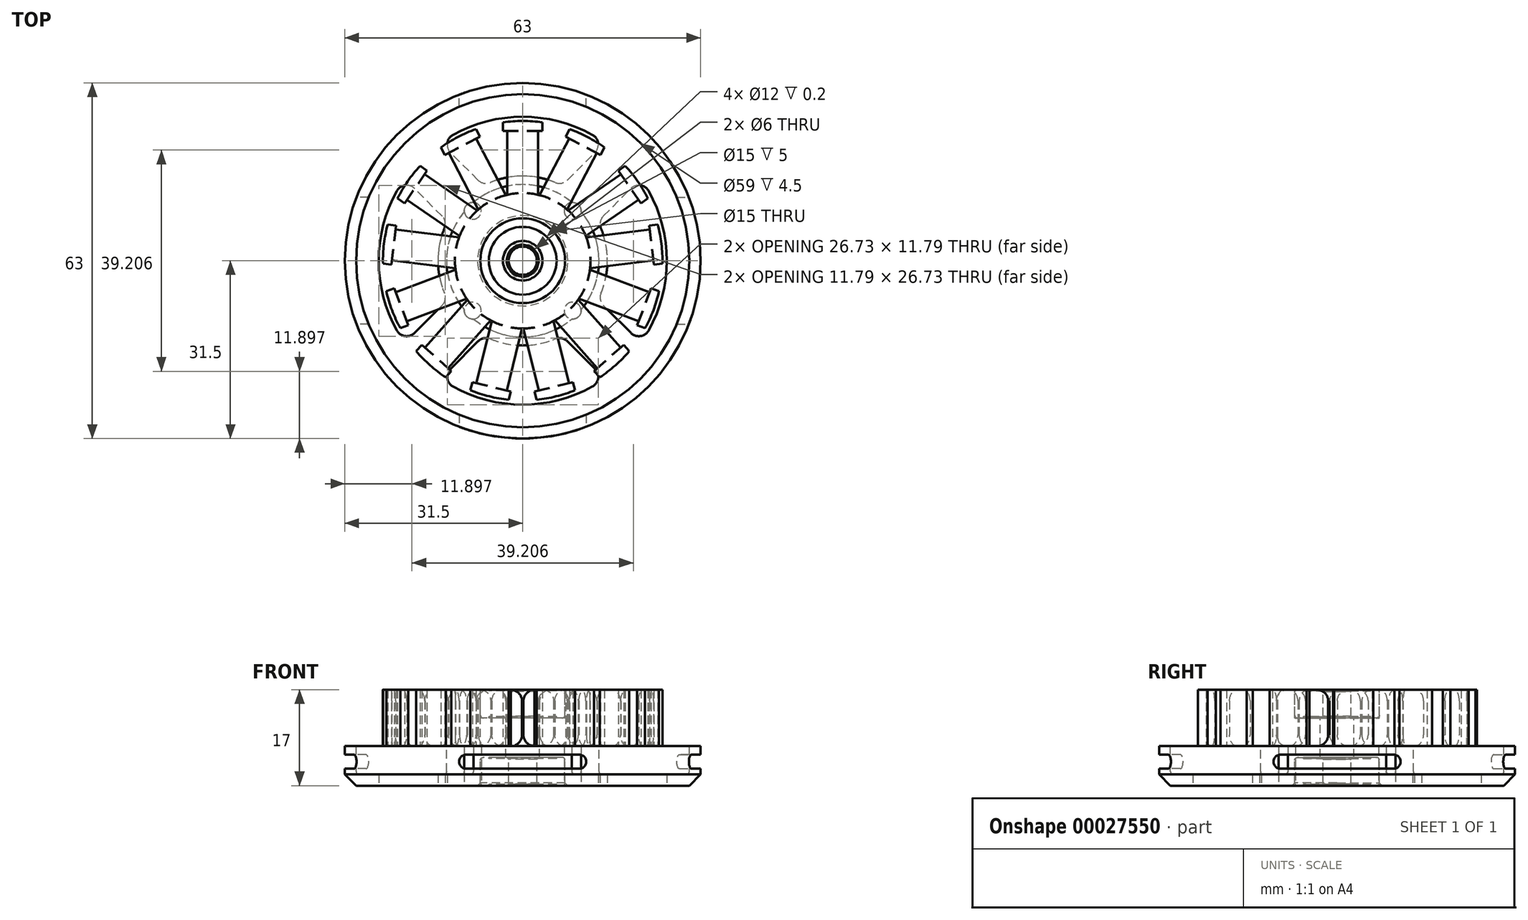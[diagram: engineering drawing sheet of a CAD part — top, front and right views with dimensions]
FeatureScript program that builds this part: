
annotation { "Feature Type Name" : "Feature", "Feature Type Description" : "" }
export const myFeature = defineFeature(function(context is Context, id is Id, definition is map)
    precondition{}
    {
        {
            var Q0;
            Q0=qCreatedBy(makeId("Front.planeOp"),FACE);
            var sketch = newSketch(context, id + "F0", { "sketchPlane" : qUnion([Q0])});
            skLineSegment(sketch, "E0", {"start": v(-31.5, 0) * mm, "end": v(-31.5, -7) * mm});
            skLineSegment(sketch, "E1", {"start": v(-31.5, -7) * mm, "end": v(-7.5, -7) * mm});
            skLineSegment(sketch, "E2", {"start": v(-7.5, -7) * mm, "end": v(-7.5, -2.5) * mm});
            skLineSegment(sketch, "E3", {"start": v(-7, -2) * mm, "end": v(-3, -2) * mm});
            skLineSegment(sketch, "E4", {"start": v(-3, -2) * mm, "end": v(-3, 0) * mm});
            skLineSegment(sketch, "E5", {"start": v(-3, 0) * mm, "end": v(-13.5, 0) * mm});
            skLineSegment(sketch, "E6", {"start": v(-13.5, 0) * mm, "end": v(-13.5, -4.5) * mm});
            skLineSegment(sketch, "E7", {"start": v(-14, -5) * mm, "end": v(-29, -5) * mm});
            skLineSegment(sketch, "E8", {"start": v(-29.5, -4.5) * mm, "end": v(-29.5, 0) * mm});
            skLineSegment(sketch, "E9", {"start": v(-29.5, 0) * mm, "end": v(-31.5, 0) * mm});
            skPoint(sketch, "E10.visualSharp", {"position": v(-29.5, -5) * mm});
            skArc(sketch, "E10.filletArc", {"start": v(-29.5, -4.5) * mm, "mid": v(-29.35, -4.85) * mm, "end": v(-29, -5) * mm});
            skPoint(sketch, "E11.visualSharp", {"position": v(-13.5, -5) * mm});
            skArc(sketch, "E11.filletArc", {"start": v(-14, -5) * mm, "mid": v(-13.65, -4.85) * mm, "end": v(-13.5, -4.5) * mm});
            skLineSegment(sketch, "E12", {"start": v(0, 0) * mm, "end": v(0, -16.71) * mm, "construction": true});
            skPoint(sketch, "E13.visualSharp", {"position": v(-7.5, -2) * mm});
            skArc(sketch, "E13.filletArc", {"start": v(-7, -2) * mm, "mid": v(-7.35, -2.15) * mm, "end": v(-7.5, -2.5) * mm});
            skSolve(sketch);
        }
        {
            var Q0;
            Q0 = qSketchRegion(id + "F0", true);
            var Q1;
            Q1=sQuery(id+"F0.wireOp",EDGE,"E12");
            revolve(context, id + "F1", {"entities" : qUnion([Q0]), "axis" : qUnion([Q1]), "revolveType" : RevolveType.FULL});
        }
        {
            var Q0;
            Q0=makeQuery(id+"F1.opRevolve","SWEPT_FACE",FACE,{"disambiguationData":[OSD([sQuery(id+"F0.wireOp",EDGE,"E1")])]});
            var sketch = newSketch(context, id + "F2", { "sketchPlane" : qUnion([Q0])});
            skArc(sketch, "E14", {"start": v(5.75, 13.86) * mm, "mid": v(0, 15) * mm, "end": v(-5.75, 13.86) * mm});
            skArc(sketch, "E15", {"start": v(12.34, 22.32) * mm, "mid": v(0, 25.5) * mm, "end": v(-12.34, 22.32) * mm});
            skLineSegment(sketch, "E16", {"start": v(0, 0) * mm, "end": v(-18.03, 18.03) * mm, "construction": true});
            skLineSegment(sketch, "E17", {"start": v(0, 0) * mm, "end": v(18.03, 18.03) * mm, "construction": true});
            skLineSegment(sketch, "E18.0", {"start": v(-7.93, 14.29) * mm, "end": v(-12.79, 19.15) * mm});
            skLineSegment(sketch, "E19.0", {"start": v(7.93, 14.29) * mm, "end": v(12.79, 19.15) * mm});
            skPoint(sketch, "E20.visualSharp", {"position": v(-14.57, 20.93) * mm});
            skArc(sketch, "E20.filletArc", {"start": v(-12.34, 22.32) * mm, "mid": v(-13.35, 20.84) * mm, "end": v(-12.79, 19.15) * mm});
            skPoint(sketch, "E21.visualSharp", {"position": v(-6.94, 13.3) * mm});
            skArc(sketch, "E21.filletArc", {"start": v(-7.93, 14.29) * mm, "mid": v(-6.9, 13.74) * mm, "end": v(-5.75, 13.86) * mm});
            skPoint(sketch, "E22.visualSharp", {"position": v(6.94, 13.3) * mm});
            skArc(sketch, "E22.filletArc", {"start": v(5.75, 13.86) * mm, "mid": v(6.9, 13.74) * mm, "end": v(7.93, 14.29) * mm});
            skPoint(sketch, "E23.visualSharp", {"position": v(14.57, 20.93) * mm});
            skArc(sketch, "E23.filletArc", {"start": v(12.79, 19.15) * mm, "mid": v(13.35, 20.84) * mm, "end": v(12.34, 22.32) * mm});
            skPoint(sketch, "E24.1.0", {"position": v(-20.93, -14.57) * mm});
            skPoint(sketch, "E24.1.1", {"position": v(-13.3, -6.94) * mm});
            skPoint(sketch, "E24.1.2", {"position": v(-13.3, 6.94) * mm});
            skPoint(sketch, "E24.1.3", {"position": v(-20.93, 14.57) * mm});
            skArc(sketch, "E24.1.4", {"start": v(-13.86, 5.75) * mm, "mid": v(-15, 0) * mm, "end": v(-13.86, -5.75) * mm});
            skArc(sketch, "E24.1.5", {"start": v(-22.32, 12.34) * mm, "mid": v(-25.5, 0) * mm, "end": v(-22.32, -12.34) * mm});
            skLineSegment(sketch, "E24.1.6", {"start": v(-14.29, -7.93) * mm, "end": v(-19.15, -12.79) * mm});
            skLineSegment(sketch, "E24.1.7", {"start": v(-14.29, 7.93) * mm, "end": v(-19.15, 12.79) * mm});
            skArc(sketch, "E24.1.8", {"start": v(-19.15, 12.79) * mm, "mid": v(-20.84, 13.35) * mm, "end": v(-22.32, 12.34) * mm});
            skArc(sketch, "E24.1.9", {"start": v(-22.32, -12.34) * mm, "mid": v(-20.84, -13.35) * mm, "end": v(-19.15, -12.79) * mm});
            skArc(sketch, "E24.1.10", {"start": v(-13.86, 5.75) * mm, "mid": v(-13.74, 6.9) * mm, "end": v(-14.29, 7.93) * mm});
            skArc(sketch, "E24.1.11", {"start": v(-14.29, -7.93) * mm, "mid": v(-13.74, -6.9) * mm, "end": v(-13.86, -5.75) * mm});
            skPoint(sketch, "E24.2.0", {"position": v(14.57, -20.93) * mm});
            skPoint(sketch, "E24.2.1", {"position": v(6.94, -13.3) * mm});
            skPoint(sketch, "E24.2.2", {"position": v(-6.94, -13.3) * mm});
            skPoint(sketch, "E24.2.3", {"position": v(-14.57, -20.93) * mm});
            skArc(sketch, "E24.2.4", {"start": v(-5.75, -13.86) * mm, "mid": v(0, -15) * mm, "end": v(5.75, -13.86) * mm});
            skArc(sketch, "E24.2.5", {"start": v(-12.34, -22.32) * mm, "mid": v(0, -25.5) * mm, "end": v(12.34, -22.32) * mm});
            skLineSegment(sketch, "E24.2.6", {"start": v(7.93, -14.29) * mm, "end": v(12.79, -19.15) * mm});
            skLineSegment(sketch, "E24.2.7", {"start": v(-7.93, -14.29) * mm, "end": v(-12.79, -19.15) * mm});
            skArc(sketch, "E24.2.8", {"start": v(-12.79, -19.15) * mm, "mid": v(-13.35, -20.84) * mm, "end": v(-12.34, -22.32) * mm});
            skArc(sketch, "E24.2.9", {"start": v(12.34, -22.32) * mm, "mid": v(13.35, -20.84) * mm, "end": v(12.79, -19.15) * mm});
            skArc(sketch, "E24.2.10", {"start": v(-5.75, -13.86) * mm, "mid": v(-6.9, -13.74) * mm, "end": v(-7.93, -14.29) * mm});
            skArc(sketch, "E24.2.11", {"start": v(7.93, -14.29) * mm, "mid": v(6.9, -13.74) * mm, "end": v(5.75, -13.86) * mm});
            skPoint(sketch, "E25.0.3.0", {"position": v(20.93, 14.57) * mm});
            skPoint(sketch, "E25.1.3.0", {"position": v(13.3, 6.94) * mm});
            skPoint(sketch, "E25.2.3.0", {"position": v(13.3, -6.94) * mm});
            skPoint(sketch, "E25.3.3.0", {"position": v(20.93, -14.57) * mm});
            skArc(sketch, "E25.4.3.0", {"start": v(13.86, -5.75) * mm, "mid": v(15, 0) * mm, "end": v(13.86, 5.75) * mm});
            skArc(sketch, "E25.8.3.0", {"start": v(22.32, -12.34) * mm, "mid": v(25.5, 0) * mm, "end": v(22.32, 12.34) * mm});
            skLineSegment(sketch, "E25.12.3.0", {"start": v(14.29, 7.93) * mm, "end": v(19.15, 12.79) * mm});
            skLineSegment(sketch, "E25.15.3.0", {"start": v(14.29, -7.93) * mm, "end": v(19.15, -12.79) * mm});
            skArc(sketch, "E25.18.3.0", {"start": v(19.15, -12.79) * mm, "mid": v(20.84, -13.35) * mm, "end": v(22.32, -12.34) * mm});
            skArc(sketch, "E25.22.3.0", {"start": v(22.32, 12.34) * mm, "mid": v(20.84, 13.35) * mm, "end": v(19.15, 12.79) * mm});
            skArc(sketch, "E25.26.3.0", {"start": v(13.86, -5.75) * mm, "mid": v(13.74, -6.9) * mm, "end": v(14.29, -7.93) * mm});
            skArc(sketch, "E25.30.3.0", {"start": v(14.29, 7.93) * mm, "mid": v(13.74, 6.9) * mm, "end": v(13.86, 5.75) * mm});
            skSolve(sketch);
        }
        {
            var Q0;
            Q0 = qSketchRegion(id + "F2", true);
            var Q1;
            Q1=makeQuery(id+"F1.opRevolve","SWEPT_FACE",FACE,{"disambiguationData":[OSD([sQuery(id+"F0.wireOp",EDGE,"E7")])]});
            extrude(context, id + "F3", {"entities" : qUnion([Q0]), "operationType" : NewBodyOperationType.REMOVE, "endBound" : BoundingType.UP_TO_SURFACE, "oppositeDirection" : true, "endBoundEntityFace" : qUnion([Q1]), "depth" : 25.4 * mm});
        }
        {
            var Q0;
            Q0=makeQuery(id+"F1.opRevolve","SWEPT_FACE",FACE,{"disambiguationData":[OSD([sQuery(id+"F0.wireOp",EDGE,"E1")])]});
            var sketch = newSketch(context, id + "F4", { "sketchPlane" : qUnion([Q0])});
            skLineSegment(sketch, "E26", {"start": v(0, 0) * mm, "end": v(-22.27, 22.27) * mm, "construction": true});
            skCircle(sketch, "E27", {"center": v(-8.84, 8.84) * mm, "radius": 1.5 * mm});
            skCircle(sketch, "E28.1.0", {"center": v(-8.84, -8.84) * mm, "radius": 1.5 * mm});
            skCircle(sketch, "E28.2.0", {"center": v(8.84, -8.84) * mm, "radius": 1.5 * mm});
            skPoint(sketch, "E28.center", {"position": v(0, 0) * mm});
            skCircle(sketch, "E29.1.3.0", {"center": v(8.84, 8.84) * mm, "radius": 1.5 * mm});
            skSolve(sketch);
        }
        {
            var Q0;
            Q0 = qSketchRegion(id + "F4", true);
            var Q1;
            Q1=makeQuery(id+"F1.opRevolve","SWEPT_FACE",FACE,{"disambiguationData":[OSD([sQuery(id+"F0.wireOp",EDGE,"E5")])]});
            extrude(context, id + "F5", {"entities" : qUnion([Q0]), "operationType" : NewBodyOperationType.REMOVE, "endBound" : BoundingType.UP_TO_SURFACE, "oppositeDirection" : true, "endBoundEntityFace" : qUnion([Q1]), "depth" : 25.4 * mm});
        }
        {
            var Q0;
            Q0=qCreatedBy(makeId("Front.planeOp"),FACE);
            cPlane(context, id + "F6", {"entities" : qUnion([Q0]), "cplaneType" : CPlaneType.OFFSET, "offset" : 38.1 * mm, "width" : 152.4 * mm, "height" : 152.4 * mm});
        }
        {
            var Q0;
            Q0=qCreatedBy(id+"F6.planeOp",FACE);
            var sketch = newSketch(context, id + "F7", { "sketchPlane" : qUnion([Q0])});
            skLineSegment(sketch, "E30.bottom", {"start": v(-10, -1.5) * mm, "end": v(10, -1.5) * mm});
            skLineSegment(sketch, "E30.top", {"start": v(-10, -4) * mm, "end": v(10, -4) * mm});
            skLineSegment(sketch, "E31", {"start": v(0, 0) * mm, "end": v(0, -7.1) * mm, "construction": true});
            skPoint(sketch, "E32", {"position": v(0, -1.5) * mm});
            skArc(sketch, "E33", {"start": v(-10, -1.5) * mm, "mid": v(-11.25, -2.75) * mm, "end": v(-10, -4) * mm});
            skArc(sketch, "E34", {"start": v(10, -4) * mm, "mid": v(11.25, -2.75) * mm, "end": v(10, -1.5) * mm});
            skSolve(sketch);
        }
        {
            var Q0;
            Q0 = qSketchRegion(id + "F7", true);
            var Q1;
            Q1=makeQuery(id+"F1.opRevolve","SWEPT_FACE",FACE,{"disambiguationData":[OSD([sQuery(id+"F0.wireOp",EDGE,"E8")])]});
            extrude(context, id + "F8", {"entities" : qUnion([Q0]), "operationType" : NewBodyOperationType.REMOVE, "endBound" : BoundingType.UP_TO_SURFACE, "oppositeDirection" : true, "endBoundEntityFace" : qUnion([Q1]), "depth" : 25.4 * mm});
        }
        {
            var Q0;
            Q0=qCreatedBy(makeId("Front.planeOp"),FACE);
            cPlane(context, id + "F9", {"entities" : qUnion([Q0]), "cplaneType" : CPlaneType.OFFSET, "offset" : 38.1 * mm, "oppositeDirection" : true, "width" : 152.4 * mm, "height" : 152.4 * mm});
        }
        {
            var Q0;
            Q0=qCreatedBy(id+"F9.planeOp",FACE);
            var sketch = newSketch(context, id + "F10", { "sketchPlane" : qUnion([Q0])});
            skLineSegment(sketch, "E35.0", {"start": v(-10, -4) * mm, "end": v(10, -4) * mm});
            skLineSegment(sketch, "E35.1", {"start": v(-10, -1.5) * mm, "end": v(10, -1.5) * mm});
            skLineSegment(sketch, "E35.2", {"start": v(-10, -4) * mm, "end": v(10, -4) * mm});
            skLineSegment(sketch, "E35.3", {"start": v(0, 0) * mm, "end": v(0, -7.1) * mm});
            skPoint(sketch, "E35.4", {"position": v(0, -1.5) * mm});
            skArc(sketch, "E35.5", {"start": v(-10, -1.5) * mm, "mid": v(-11.25, -2.75) * mm, "end": v(-10, -4) * mm});
            skArc(sketch, "E35.6", {"start": v(10, -4) * mm, "mid": v(11.25, -2.75) * mm, "end": v(10, -1.5) * mm});
            skSolve(sketch);
        }
        {
            var Q0;
            Q0 = qSketchRegion(id + "F10", true);
            var Q1;
            Q1=makeQuery(id+"F1.opRevolve","SWEPT_FACE",FACE,{"disambiguationData":[OSD([sQuery(id+"F0.wireOp",EDGE,"E8")])]});
            extrude(context, id + "F11", {"entities" : qUnion([Q0]), "operationType" : NewBodyOperationType.REMOVE, "endBound" : BoundingType.UP_TO_SURFACE, "endBoundEntityFace" : qUnion([Q1]), "depth" : 25.4 * mm});
        }
        {
            var Q0;
            Q0=qCreatedBy(makeId("Right.planeOp"),FACE);
            cPlane(context, id + "F12", {"entities" : qUnion([Q0]), "cplaneType" : CPlaneType.OFFSET, "offset" : 38.1 * mm, "width" : 152.4 * mm, "height" : 152.4 * mm});
        }
        {
            var Q0;
            Q0=qCreatedBy(id+"F12.planeOp",FACE);
            var sketch = newSketch(context, id + "F13", { "sketchPlane" : qUnion([Q0])});
            skLineSegment(sketch, "E36", {"start": v(0, 0) * mm, "end": v(0, -10.16) * mm, "construction": true});
            skLineSegment(sketch, "E37.bottom", {"start": v(-10, -1.5) * mm, "end": v(10, -1.5) * mm});
            skLineSegment(sketch, "E37.top", {"start": v(-10, -4) * mm, "end": v(10, -4) * mm});
            skPoint(sketch, "E38", {"position": v(0, -4) * mm});
            skArc(sketch, "E39", {"start": v(-10, -1.5) * mm, "mid": v(-11.25, -2.75) * mm, "end": v(-10, -4) * mm});
            skArc(sketch, "E40", {"start": v(10, -4) * mm, "mid": v(11.25, -2.75) * mm, "end": v(10, -1.5) * mm});
            skSolve(sketch);
        }
        {
            var Q0;
            Q0 = qSketchRegion(id + "F13", true);
            var Q1;
            Q1=makeQuery(id+"F1.opRevolve","SWEPT_FACE",FACE,{"disambiguationData":[OSD([sQuery(id+"F0.wireOp",EDGE,"E8")])]});
            extrude(context, id + "F14", {"entities" : qUnion([Q0]), "operationType" : NewBodyOperationType.REMOVE, "endBound" : BoundingType.UP_TO_SURFACE, "oppositeDirection" : true, "endBoundEntityFace" : qUnion([Q1]), "depth" : 25.4 * mm});
        }
        {
            var Q0;
            Q0=qCreatedBy(makeId("Right.planeOp"),FACE);
            cPlane(context, id + "F15", {"entities" : qUnion([Q0]), "cplaneType" : CPlaneType.OFFSET, "offset" : 38.1 * mm, "oppositeDirection" : true, "width" : 152.4 * mm, "height" : 152.4 * mm});
        }
        {
            var Q0;
            Q0=qCreatedBy(id+"F15.planeOp",FACE);
            var sketch = newSketch(context, id + "F16", { "sketchPlane" : qUnion([Q0])});
            skLineSegment(sketch, "E41.0", {"start": v(0, 0) * mm, "end": v(0, -10.16) * mm});
            skLineSegment(sketch, "E41.1", {"start": v(-10, -1.5) * mm, "end": v(10, -1.5) * mm});
            skLineSegment(sketch, "E41.2", {"start": v(-10, -4) * mm, "end": v(10, -4) * mm});
            skPoint(sketch, "E41.3", {"position": v(0, -4) * mm});
            skArc(sketch, "E41.4", {"start": v(-10, -1.5) * mm, "mid": v(-11.25, -2.75) * mm, "end": v(-10, -4) * mm});
            skArc(sketch, "E41.5", {"start": v(10, -4) * mm, "mid": v(11.25, -2.75) * mm, "end": v(10, -1.5) * mm});
            skSolve(sketch);
        }
        {
            var Q0;
            Q0 = qSketchRegion(id + "F16", true);
            var Q1;
            Q1=makeQuery(id+"F1.opRevolve","SWEPT_FACE",FACE,{"disambiguationData":[OSD([sQuery(id+"F0.wireOp",EDGE,"E8")])]});
            extrude(context, id + "F17", {"entities" : qUnion([Q0]), "operationType" : NewBodyOperationType.REMOVE, "endBound" : BoundingType.UP_TO_SURFACE, "endBoundEntityFace" : qUnion([Q1]), "depth" : 25.4 * mm});
        }
        {
            var Q0;
            Q0=makeQuery(id+"F1.opRevolve","SWEPT_EDGE",EDGE,{"disambiguationData":[OSD([sQuery(id+"F0.wireOp",EDGE,"E0"),sQuery(id+"F0.wireOp",EDGE,"E1")])]});
            chamfer(context, id + "F18", {"entities" : qUnion([Q0]), "width" : 2 * mm, "tangentPropagation" : true});
        }
        {
            var Q0;
            Q0=makeQuery(id+"F1.opRevolve","SWEPT_EDGE",EDGE,{"disambiguationData":[OSD([sQuery(id+"F0.wireOp",EDGE,"E1"),sQuery(id+"F0.wireOp",EDGE,"E2")])]});
            var Q1;
            Q1=makeQuery(id+"F3.boolean.opBoolean","COPY",EDGE,{"derivedFrom":makeQuery(id+"F3.opExtrude","CAP_EDGE",EDGE,{"disambiguationData":[OSD([sQuery(id+"F2.wireOp",EDGE,"E18.0")])],"isStart":true})});
            var Q2;
            Q2=makeQuery(id+"F3.boolean.opBoolean","COPY",EDGE,{"derivedFrom":makeQuery(id+"F3.opExtrude","CAP_EDGE",EDGE,{"disambiguationData":[OSD([sQuery(id+"F2.wireOp",EDGE,"E24.1.7")])],"isStart":true})});
            var Q3;
            Q3=makeQuery(id+"F3.boolean.opBoolean","COPY",EDGE,{"derivedFrom":makeQuery(id+"F3.opExtrude","CAP_EDGE",EDGE,{"disambiguationData":[OSD([sQuery(id+"F2.wireOp",EDGE,"E24.2.7")])],"isStart":true})});
            var Q4;
            Q4=makeQuery(id+"F3.boolean.opBoolean","COPY",EDGE,{"derivedFrom":makeQuery(id+"F3.opExtrude","CAP_EDGE",EDGE,{"disambiguationData":[OSD([sQuery(id+"F2.wireOp",EDGE,"E25.15.3.0")])],"isStart":true})});
            chamfer(context, id + "F19", {"entities" : qUnion([Q0, Q1, Q2, Q3, Q4]), "width" : .5 * mm, "tangentPropagation" : true});
        }
        {
            var Q0;
            Q0=makeQuery(id+"F1.opRevolve","SWEPT_FACE",FACE,{"disambiguationData":[OSD([sQuery(id+"F0.wireOp",EDGE,"E5")])]});
            var sketch = newSketch(context, id + "F20", { "sketchPlane" : qUnion([Q0])});
            skCircle(sketch, "E42", {"center": v(0, 0) * mm, "radius": 12 * mm});
            skArc(sketch, "E43", {"start": v(3.5, 24.5) * mm, "mid": v(0, 24.75) * mm, "end": v(-3.5, 24.5) * mm});
            skLineSegment(sketch, "E44", {"start": v(0, 0) * mm, "end": v(0, 24.75) * mm, "construction": true});
            skLineSegment(sketch, "E45", {"start": v(-3.5, 24.5) * mm, "end": v(-3.5, 23) * mm});
            skLineSegment(sketch, "E46", {"start": v(-3.5, 23) * mm, "end": v(-2.75, 23) * mm});
            skLineSegment(sketch, "E47", {"start": v(-2.75, 23) * mm, "end": v(-2.75, 11.68) * mm});
            skLineSegment(sketch, "E48.MirrorCS", {"start": v(3.5, 23) * mm, "end": v(2.75, 23) * mm});
            skLineSegment(sketch, "E49.MirrorCS", {"start": v(2.75, 23) * mm, "end": v(2.75, 11.68) * mm});
            skLineSegment(sketch, "E50.MirrorCS", {"start": v(3.5, 24.5) * mm, "end": v(3.5, 23) * mm});
            skLineSegment(sketch, "E51.1.0", {"start": v(-8.29, 23.32) * mm, "end": v(-7.6, 22) * mm});
            skLineSegment(sketch, "E51.1.1", {"start": v(-8.25, 21.64) * mm, "end": v(-3, 11.62) * mm});
            skLineSegment(sketch, "E51.1.2", {"start": v(-13.12, 19.09) * mm, "end": v(-7.86, 9.06) * mm});
            skLineSegment(sketch, "E51.1.3", {"start": v(-14.49, 20.07) * mm, "end": v(-13.79, 18.74) * mm});
            skArc(sketch, "E51.1.4", {"start": v(-8.29, 23.32) * mm, "mid": v(-11.5, 21.92) * mm, "end": v(-14.49, 20.07) * mm});
            skLineSegment(sketch, "E51.1.5", {"start": v(-7.6, 22) * mm, "end": v(-8.25, 21.64) * mm});
            skLineSegment(sketch, "E51.1.6", {"start": v(-13.79, 18.74) * mm, "end": v(-13.12, 19.09) * mm});
            skLineSegment(sketch, "E51.2.0", {"start": v(-18.18, 16.8) * mm, "end": v(-16.94, 15.95) * mm});
            skLineSegment(sketch, "E51.2.1", {"start": v(-17.37, 15.33) * mm, "end": v(-8.05, 8.9) * mm});
            skLineSegment(sketch, "E51.2.2", {"start": v(-20.5, 10.8) * mm, "end": v(-11.18, 4.37) * mm});
            skLineSegment(sketch, "E51.2.3", {"start": v(-22.15, 11.04) * mm, "end": v(-20.92, 10.19) * mm});
            skArc(sketch, "E51.2.4", {"start": v(-18.18, 16.8) * mm, "mid": v(-20.37, 14.06) * mm, "end": v(-22.15, 11.04) * mm});
            skLineSegment(sketch, "E51.2.5", {"start": v(-16.94, 15.95) * mm, "end": v(-17.37, 15.33) * mm});
            skLineSegment(sketch, "E51.2.6", {"start": v(-20.92, 10.19) * mm, "end": v(-20.5, 10.8) * mm});
            skLineSegment(sketch, "E52.2.3.0", {"start": v(-23.9, 6.43) * mm, "end": v(-22.41, 6.25) * mm});
            skLineSegment(sketch, "E52.3.3.0", {"start": v(-22.5, 5.5) * mm, "end": v(-11.26, 4.14) * mm});
            skLineSegment(sketch, "E52.6.3.0", {"start": v(-23.17, 0.04) * mm, "end": v(-11.93, -1.32) * mm});
            skLineSegment(sketch, "E52.9.3.0", {"start": v(-24.74, -0.52) * mm, "end": v(-23.26, -0.7) * mm});
            skArc(sketch, "E52.12.3.0", {"start": v(-23.9, 6.43) * mm, "mid": v(-24.57, 2.98) * mm, "end": v(-24.74, -0.52) * mm});
            skLineSegment(sketch, "E52.16.3.0", {"start": v(-22.41, 6.25) * mm, "end": v(-22.5, 5.5) * mm});
            skLineSegment(sketch, "E52.19.3.0", {"start": v(-23.26, -0.7) * mm, "end": v(-23.17, 0.04) * mm});
            skLineSegment(sketch, "E52.2.4.0", {"start": v(-24.15, -5.42) * mm, "end": v(-22.75, -4.88) * mm});
            skLineSegment(sketch, "E52.3.4.0", {"start": v(-22.48, -5.59) * mm, "end": v(-11.9, -1.57) * mm});
            skLineSegment(sketch, "E52.6.4.0", {"start": v(-20.53, -10.73) * mm, "end": v(-9.95, -6.71) * mm});
            skLineSegment(sketch, "E52.9.4.0", {"start": v(-21.67, -11.96) * mm, "end": v(-20.27, -11.43) * mm});
            skArc(sketch, "E52.12.4.0", {"start": v(-24.15, -5.42) * mm, "mid": v(-23.14, -8.78) * mm, "end": v(-21.67, -11.96) * mm});
            skLineSegment(sketch, "E52.16.4.0", {"start": v(-22.75, -4.88) * mm, "end": v(-22.48, -5.59) * mm});
            skLineSegment(sketch, "E52.19.4.0", {"start": v(-20.27, -11.43) * mm, "end": v(-20.53, -10.73) * mm});
            skLineSegment(sketch, "E52.2.5.0", {"start": v(-18.87, -16.02) * mm, "end": v(-17.87, -14.9) * mm});
            skLineSegment(sketch, "E52.3.5.0", {"start": v(-17.31, -15.4) * mm, "end": v(-9.8, -6.92) * mm});
            skLineSegment(sketch, "E52.6.5.0", {"start": v(-13.2, -19.04) * mm, "end": v(-5.69, -10.57) * mm});
            skLineSegment(sketch, "E52.9.5.0", {"start": v(-13.63, -20.66) * mm, "end": v(-12.63, -19.54) * mm});
            skArc(sketch, "E52.12.5.0", {"start": v(-18.87, -16.02) * mm, "mid": v(-16.41, -18.53) * mm, "end": v(-13.63, -20.66) * mm});
            skLineSegment(sketch, "E52.16.5.0", {"start": v(-17.87, -14.9) * mm, "end": v(-17.31, -15.4) * mm});
            skLineSegment(sketch, "E52.19.5.0", {"start": v(-12.63, -19.54) * mm, "end": v(-13.2, -19.04) * mm});
            skLineSegment(sketch, "E52.2.6.0", {"start": v(-9.26, -22.95) * mm, "end": v(-8.9, -21.5) * mm});
            skLineSegment(sketch, "E52.3.6.0", {"start": v(-8.17, -21.67) * mm, "end": v(-5.47, -10.68) * mm});
            skLineSegment(sketch, "E52.6.6.0", {"start": v(-2.83, -23) * mm, "end": v(-0.13, -12) * mm});
            skLineSegment(sketch, "E52.9.6.0", {"start": v(-2.47, -24.63) * mm, "end": v(-2.1, -23.17) * mm});
            skArc(sketch, "E52.12.6.0", {"start": v(-9.26, -22.95) * mm, "mid": v(-5.92, -24.03) * mm, "end": v(-2.47, -24.63) * mm});
            skLineSegment(sketch, "E52.16.6.0", {"start": v(-8.9, -21.5) * mm, "end": v(-8.17, -21.67) * mm});
            skLineSegment(sketch, "E52.19.6.0", {"start": v(-2.1, -23.17) * mm, "end": v(-2.83, -23) * mm});
            skLineSegment(sketch, "E52.2.7.0", {"start": v(2.47, -24.63) * mm, "end": v(2.1, -23.17) * mm});
            skLineSegment(sketch, "E52.3.7.0", {"start": v(2.83, -23) * mm, "end": v(0.13, -12) * mm});
            skLineSegment(sketch, "E52.6.7.0", {"start": v(8.17, -21.67) * mm, "end": v(5.47, -10.68) * mm});
            skLineSegment(sketch, "E52.9.7.0", {"start": v(9.26, -22.95) * mm, "end": v(8.9, -21.5) * mm});
            skArc(sketch, "E52.12.7.0", {"start": v(2.47, -24.63) * mm, "mid": v(5.92, -24.03) * mm, "end": v(9.26, -22.95) * mm});
            skLineSegment(sketch, "E52.16.7.0", {"start": v(2.1, -23.17) * mm, "end": v(2.83, -23) * mm});
            skLineSegment(sketch, "E52.19.7.0", {"start": v(8.9, -21.5) * mm, "end": v(8.17, -21.67) * mm});
            skLineSegment(sketch, "E52.2.8.0", {"start": v(13.63, -20.66) * mm, "end": v(12.63, -19.54) * mm});
            skLineSegment(sketch, "E52.3.8.0", {"start": v(13.2, -19.04) * mm, "end": v(5.69, -10.57) * mm});
            skLineSegment(sketch, "E52.6.8.0", {"start": v(17.31, -15.4) * mm, "end": v(9.8, -6.92) * mm});
            skLineSegment(sketch, "E52.9.8.0", {"start": v(18.87, -16.02) * mm, "end": v(17.87, -14.9) * mm});
            skArc(sketch, "E52.12.8.0", {"start": v(13.63, -20.66) * mm, "mid": v(16.41, -18.53) * mm, "end": v(18.87, -16.02) * mm});
            skLineSegment(sketch, "E52.16.8.0", {"start": v(12.63, -19.54) * mm, "end": v(13.2, -19.04) * mm});
            skLineSegment(sketch, "E52.19.8.0", {"start": v(17.87, -14.9) * mm, "end": v(17.31, -15.4) * mm});
            skLineSegment(sketch, "E52.2.9.0", {"start": v(21.67, -11.96) * mm, "end": v(20.27, -11.43) * mm});
            skLineSegment(sketch, "E52.3.9.0", {"start": v(20.53, -10.73) * mm, "end": v(9.95, -6.71) * mm});
            skLineSegment(sketch, "E52.6.9.0", {"start": v(22.48, -5.59) * mm, "end": v(11.9, -1.57) * mm});
            skLineSegment(sketch, "E52.9.9.0", {"start": v(24.15, -5.42) * mm, "end": v(22.75, -4.88) * mm});
            skArc(sketch, "E52.12.9.0", {"start": v(21.67, -11.96) * mm, "mid": v(23.14, -8.78) * mm, "end": v(24.15, -5.42) * mm});
            skLineSegment(sketch, "E52.16.9.0", {"start": v(20.27, -11.43) * mm, "end": v(20.53, -10.73) * mm});
            skLineSegment(sketch, "E52.19.9.0", {"start": v(22.75, -4.88) * mm, "end": v(22.48, -5.59) * mm});
            skLineSegment(sketch, "E52.2.10.0", {"start": v(24.74, -0.52) * mm, "end": v(23.26, -0.7) * mm});
            skLineSegment(sketch, "E52.3.10.0", {"start": v(23.17, 0.04) * mm, "end": v(11.93, -1.32) * mm});
            skLineSegment(sketch, "E52.6.10.0", {"start": v(22.5, 5.5) * mm, "end": v(11.26, 4.14) * mm});
            skLineSegment(sketch, "E52.9.10.0", {"start": v(23.9, 6.43) * mm, "end": v(22.41, 6.25) * mm});
            skArc(sketch, "E52.12.10.0", {"start": v(24.74, -0.52) * mm, "mid": v(24.57, 2.98) * mm, "end": v(23.9, 6.43) * mm});
            skLineSegment(sketch, "E52.16.10.0", {"start": v(23.26, -0.7) * mm, "end": v(23.17, 0.04) * mm});
            skLineSegment(sketch, "E52.19.10.0", {"start": v(22.41, 6.25) * mm, "end": v(22.5, 5.5) * mm});
            skLineSegment(sketch, "E52.2.11.0", {"start": v(22.15, 11.04) * mm, "end": v(20.92, 10.19) * mm});
            skLineSegment(sketch, "E52.3.11.0", {"start": v(20.5, 10.8) * mm, "end": v(11.18, 4.37) * mm});
            skLineSegment(sketch, "E52.6.11.0", {"start": v(17.37, 15.33) * mm, "end": v(8.05, 8.9) * mm});
            skLineSegment(sketch, "E52.9.11.0", {"start": v(18.18, 16.8) * mm, "end": v(16.94, 15.95) * mm});
            skArc(sketch, "E52.12.11.0", {"start": v(22.15, 11.04) * mm, "mid": v(20.37, 14.06) * mm, "end": v(18.18, 16.8) * mm});
            skLineSegment(sketch, "E52.16.11.0", {"start": v(20.92, 10.19) * mm, "end": v(20.5, 10.8) * mm});
            skLineSegment(sketch, "E52.19.11.0", {"start": v(16.94, 15.95) * mm, "end": v(17.37, 15.33) * mm});
            skLineSegment(sketch, "E52.2.12.0", {"start": v(14.49, 20.07) * mm, "end": v(13.79, 18.74) * mm});
            skLineSegment(sketch, "E52.3.12.0", {"start": v(13.12, 19.09) * mm, "end": v(7.86, 9.06) * mm});
            skLineSegment(sketch, "E52.6.12.0", {"start": v(8.25, 21.64) * mm, "end": v(3, 11.62) * mm});
            skLineSegment(sketch, "E52.9.12.0", {"start": v(8.29, 23.32) * mm, "end": v(7.6, 22) * mm});
            skArc(sketch, "E52.12.12.0", {"start": v(14.49, 20.07) * mm, "mid": v(11.5, 21.92) * mm, "end": v(8.29, 23.32) * mm});
            skLineSegment(sketch, "E52.16.12.0", {"start": v(13.79, 18.74) * mm, "end": v(13.12, 19.09) * mm});
            skLineSegment(sketch, "E52.19.12.0", {"start": v(7.6, 22) * mm, "end": v(8.25, 21.64) * mm});
            skSolve(sketch);
        }
        {
            var Q0;
            Q0 = qSketchRegion(id + "F20", true);
            extrude(context, id + "F21", {"entities" : qUnion([Q0]), "depth" : 10 * mm});
        }
        {
            var Q0;
            Q0=makeQuery(id+"F21.opExtrude","CAP_FACE",FACE,{"disambiguationData":[OSD([sQuery(id+"F20.wireOp",EDGE,"E42"),sQuery(id+"F20.wireOp",EDGE,"E43"),sQuery(id+"F20.wireOp",EDGE,"E45"),sQuery(id+"F20.wireOp",EDGE,"E46"),sQuery(id+"F20.wireOp",EDGE,"E47"),sQuery(id+"F20.wireOp",EDGE,"E48.MirrorCS"),sQuery(id+"F20.wireOp",EDGE,"E49.MirrorCS"),sQuery(id+"F20.wireOp",EDGE,"E50.MirrorCS"),sQuery(id+"F20.wireOp",EDGE,"E51.1.0"),sQuery(id+"F20.wireOp",EDGE,"E51.1.1"),sQuery(id+"F20.wireOp",EDGE,"E51.1.2"),sQuery(id+"F20.wireOp",EDGE,"E51.1.3"),sQuery(id+"F20.wireOp",EDGE,"E51.1.4"),sQuery(id+"F20.wireOp",EDGE,"E51.1.5"),sQuery(id+"F20.wireOp",EDGE,"E51.1.6"),sQuery(id+"F20.wireOp",EDGE,"E51.2.0"),sQuery(id+"F20.wireOp",EDGE,"E51.2.1"),sQuery(id+"F20.wireOp",EDGE,"E51.2.2"),sQuery(id+"F20.wireOp",EDGE,"E51.2.3"),sQuery(id+"F20.wireOp",EDGE,"E51.2.4"),sQuery(id+"F20.wireOp",EDGE,"E51.2.5"),sQuery(id+"F20.wireOp",EDGE,"E51.2.6"),sQuery(id+"F20.wireOp",EDGE,"E52.2.3.0"),sQuery(id+"F20.wireOp",EDGE,"E52.3.3.0"),sQuery(id+"F20.wireOp",EDGE,"E52.6.3.0"),sQuery(id+"F20.wireOp",EDGE,"E52.9.3.0"),sQuery(id+"F20.wireOp",EDGE,"E52.12.3.0"),sQuery(id+"F20.wireOp",EDGE,"E52.16.3.0"),sQuery(id+"F20.wireOp",EDGE,"E52.19.3.0"),sQuery(id+"F20.wireOp",EDGE,"E52.2.4.0"),sQuery(id+"F20.wireOp",EDGE,"E52.3.4.0"),sQuery(id+"F20.wireOp",EDGE,"E52.6.4.0"),sQuery(id+"F20.wireOp",EDGE,"E52.9.4.0"),sQuery(id+"F20.wireOp",EDGE,"E52.12.4.0"),sQuery(id+"F20.wireOp",EDGE,"E52.16.4.0"),sQuery(id+"F20.wireOp",EDGE,"E52.19.4.0"),sQuery(id+"F20.wireOp",EDGE,"E52.2.5.0"),sQuery(id+"F20.wireOp",EDGE,"E52.3.5.0"),sQuery(id+"F20.wireOp",EDGE,"E52.6.5.0"),sQuery(id+"F20.wireOp",EDGE,"E52.9.5.0"),sQuery(id+"F20.wireOp",EDGE,"E52.12.5.0"),sQuery(id+"F20.wireOp",EDGE,"E52.16.5.0"),sQuery(id+"F20.wireOp",EDGE,"E52.19.5.0"),sQuery(id+"F20.wireOp",EDGE,"E52.2.6.0"),sQuery(id+"F20.wireOp",EDGE,"E52.3.6.0"),sQuery(id+"F20.wireOp",EDGE,"E52.6.6.0"),sQuery(id+"F20.wireOp",EDGE,"E52.9.6.0"),sQuery(id+"F20.wireOp",EDGE,"E52.12.6.0"),sQuery(id+"F20.wireOp",EDGE,"E52.16.6.0"),sQuery(id+"F20.wireOp",EDGE,"E52.19.6.0"),sQuery(id+"F20.wireOp",EDGE,"E52.2.7.0"),sQuery(id+"F20.wireOp",EDGE,"E52.3.7.0"),sQuery(id+"F20.wireOp",EDGE,"E52.6.7.0"),sQuery(id+"F20.wireOp",EDGE,"E52.9.7.0"),sQuery(id+"F20.wireOp",EDGE,"E52.12.7.0"),sQuery(id+"F20.wireOp",EDGE,"E52.16.7.0"),sQuery(id+"F20.wireOp",EDGE,"E52.19.7.0"),sQuery(id+"F20.wireOp",EDGE,"E52.2.8.0"),sQuery(id+"F20.wireOp",EDGE,"E52.3.8.0"),sQuery(id+"F20.wireOp",EDGE,"E52.6.8.0"),sQuery(id+"F20.wireOp",EDGE,"E52.9.8.0"),sQuery(id+"F20.wireOp",EDGE,"E52.12.8.0"),sQuery(id+"F20.wireOp",EDGE,"E52.16.8.0"),sQuery(id+"F20.wireOp",EDGE,"E52.19.8.0"),sQuery(id+"F20.wireOp",EDGE,"E52.2.9.0"),sQuery(id+"F20.wireOp",EDGE,"E52.3.9.0"),sQuery(id+"F20.wireOp",EDGE,"E52.6.9.0"),sQuery(id+"F20.wireOp",EDGE,"E52.9.9.0"),sQuery(id+"F20.wireOp",EDGE,"E52.12.9.0"),sQuery(id+"F20.wireOp",EDGE,"E52.16.9.0"),sQuery(id+"F20.wireOp",EDGE,"E52.19.9.0"),sQuery(id+"F20.wireOp",EDGE,"E52.2.10.0"),sQuery(id+"F20.wireOp",EDGE,"E52.3.10.0"),sQuery(id+"F20.wireOp",EDGE,"E52.6.10.0"),sQuery(id+"F20.wireOp",EDGE,"E52.9.10.0"),sQuery(id+"F20.wireOp",EDGE,"E52.12.10.0"),sQuery(id+"F20.wireOp",EDGE,"E52.16.10.0"),sQuery(id+"F20.wireOp",EDGE,"E52.19.10.0"),sQuery(id+"F20.wireOp",EDGE,"E52.2.11.0"),sQuery(id+"F20.wireOp",EDGE,"E52.3.11.0"),sQuery(id+"F20.wireOp",EDGE,"E52.6.11.0"),sQuery(id+"F20.wireOp",EDGE,"E52.9.11.0"),sQuery(id+"F20.wireOp",EDGE,"E52.12.11.0"),sQuery(id+"F20.wireOp",EDGE,"E52.16.11.0"),sQuery(id+"F20.wireOp",EDGE,"E52.19.11.0"),sQuery(id+"F20.wireOp",EDGE,"E52.2.12.0"),sQuery(id+"F20.wireOp",EDGE,"E52.3.12.0"),sQuery(id+"F20.wireOp",EDGE,"E52.6.12.0"),sQuery(id+"F20.wireOp",EDGE,"E52.9.12.0"),sQuery(id+"F20.wireOp",EDGE,"E52.12.12.0"),sQuery(id+"F20.wireOp",EDGE,"E52.16.12.0"),sQuery(id+"F20.wireOp",EDGE,"E52.19.12.0")])],"isStart":false});
            var sketch = newSketch(context, id + "F22", { "sketchPlane" : qUnion([Q0])});
            skCircle(sketch, "E53", {"center": v(0, 0) * mm, "radius": 7.5 * mm});
            skSolve(sketch);
        }
        {
            var Q0;
            Q0 = qSketchRegion(id + "F22", true);
            extrude(context, id + "F23", {"entities" : qUnion([Q0]), "operationType" : NewBodyOperationType.REMOVE, "oppositeDirection" : true, "depth" : 5 * mm});
        }
        {
            var Q0;
            Q0=makeQuery(id+"F23.boolean.opBoolean","COPY",FACE,{"derivedFrom":makeQuery(id+"F23.opExtrude","CAP_FACE",FACE,{"disambiguationData":[OSD([sQuery(id+"F22.wireOp",EDGE,"E53")])],"isStart":false})});
            var sketch = newSketch(context, id + "F24", { "sketchPlane" : qUnion([Q0])});
            skCircle(sketch, "E54", {"center": v(0, 0) * mm, "radius": 3 * mm});
            skSolve(sketch);
        }
        {
            var Q0;
            Q0 = qSketchRegion(id + "F24", true);
            var Q1;
            Q1=makeQuery(id+"F21.opExtrude","CAP_FACE",FACE,{"disambiguationData":[OSD([sQuery(id+"F20.wireOp",EDGE,"E42"),sQuery(id+"F20.wireOp",EDGE,"E43"),sQuery(id+"F20.wireOp",EDGE,"E45"),sQuery(id+"F20.wireOp",EDGE,"E46"),sQuery(id+"F20.wireOp",EDGE,"E47"),sQuery(id+"F20.wireOp",EDGE,"E48.MirrorCS"),sQuery(id+"F20.wireOp",EDGE,"E49.MirrorCS"),sQuery(id+"F20.wireOp",EDGE,"E50.MirrorCS"),sQuery(id+"F20.wireOp",EDGE,"E51.1.0"),sQuery(id+"F20.wireOp",EDGE,"E51.1.1"),sQuery(id+"F20.wireOp",EDGE,"E51.1.2"),sQuery(id+"F20.wireOp",EDGE,"E51.1.3"),sQuery(id+"F20.wireOp",EDGE,"E51.1.4"),sQuery(id+"F20.wireOp",EDGE,"E51.1.5"),sQuery(id+"F20.wireOp",EDGE,"E51.1.6"),sQuery(id+"F20.wireOp",EDGE,"E51.2.0"),sQuery(id+"F20.wireOp",EDGE,"E51.2.1"),sQuery(id+"F20.wireOp",EDGE,"E51.2.2"),sQuery(id+"F20.wireOp",EDGE,"E51.2.3"),sQuery(id+"F20.wireOp",EDGE,"E51.2.4"),sQuery(id+"F20.wireOp",EDGE,"E51.2.5"),sQuery(id+"F20.wireOp",EDGE,"E51.2.6"),sQuery(id+"F20.wireOp",EDGE,"E52.2.3.0"),sQuery(id+"F20.wireOp",EDGE,"E52.3.3.0"),sQuery(id+"F20.wireOp",EDGE,"E52.6.3.0"),sQuery(id+"F20.wireOp",EDGE,"E52.9.3.0"),sQuery(id+"F20.wireOp",EDGE,"E52.12.3.0"),sQuery(id+"F20.wireOp",EDGE,"E52.16.3.0"),sQuery(id+"F20.wireOp",EDGE,"E52.19.3.0"),sQuery(id+"F20.wireOp",EDGE,"E52.2.4.0"),sQuery(id+"F20.wireOp",EDGE,"E52.3.4.0"),sQuery(id+"F20.wireOp",EDGE,"E52.6.4.0"),sQuery(id+"F20.wireOp",EDGE,"E52.9.4.0"),sQuery(id+"F20.wireOp",EDGE,"E52.12.4.0"),sQuery(id+"F20.wireOp",EDGE,"E52.16.4.0"),sQuery(id+"F20.wireOp",EDGE,"E52.19.4.0"),sQuery(id+"F20.wireOp",EDGE,"E52.2.5.0"),sQuery(id+"F20.wireOp",EDGE,"E52.3.5.0"),sQuery(id+"F20.wireOp",EDGE,"E52.6.5.0"),sQuery(id+"F20.wireOp",EDGE,"E52.9.5.0"),sQuery(id+"F20.wireOp",EDGE,"E52.12.5.0"),sQuery(id+"F20.wireOp",EDGE,"E52.16.5.0"),sQuery(id+"F20.wireOp",EDGE,"E52.19.5.0"),sQuery(id+"F20.wireOp",EDGE,"E52.2.6.0"),sQuery(id+"F20.wireOp",EDGE,"E52.3.6.0"),sQuery(id+"F20.wireOp",EDGE,"E52.6.6.0"),sQuery(id+"F20.wireOp",EDGE,"E52.9.6.0"),sQuery(id+"F20.wireOp",EDGE,"E52.12.6.0"),sQuery(id+"F20.wireOp",EDGE,"E52.16.6.0"),sQuery(id+"F20.wireOp",EDGE,"E52.19.6.0"),sQuery(id+"F20.wireOp",EDGE,"E52.2.7.0"),sQuery(id+"F20.wireOp",EDGE,"E52.3.7.0"),sQuery(id+"F20.wireOp",EDGE,"E52.6.7.0"),sQuery(id+"F20.wireOp",EDGE,"E52.9.7.0"),sQuery(id+"F20.wireOp",EDGE,"E52.12.7.0"),sQuery(id+"F20.wireOp",EDGE,"E52.16.7.0"),sQuery(id+"F20.wireOp",EDGE,"E52.19.7.0"),sQuery(id+"F20.wireOp",EDGE,"E52.2.8.0"),sQuery(id+"F20.wireOp",EDGE,"E52.3.8.0"),sQuery(id+"F20.wireOp",EDGE,"E52.6.8.0"),sQuery(id+"F20.wireOp",EDGE,"E52.9.8.0"),sQuery(id+"F20.wireOp",EDGE,"E52.12.8.0"),sQuery(id+"F20.wireOp",EDGE,"E52.16.8.0"),sQuery(id+"F20.wireOp",EDGE,"E52.19.8.0"),sQuery(id+"F20.wireOp",EDGE,"E52.2.9.0"),sQuery(id+"F20.wireOp",EDGE,"E52.3.9.0"),sQuery(id+"F20.wireOp",EDGE,"E52.6.9.0"),sQuery(id+"F20.wireOp",EDGE,"E52.9.9.0"),sQuery(id+"F20.wireOp",EDGE,"E52.12.9.0"),sQuery(id+"F20.wireOp",EDGE,"E52.16.9.0"),sQuery(id+"F20.wireOp",EDGE,"E52.19.9.0"),sQuery(id+"F20.wireOp",EDGE,"E52.2.10.0"),sQuery(id+"F20.wireOp",EDGE,"E52.3.10.0"),sQuery(id+"F20.wireOp",EDGE,"E52.6.10.0"),sQuery(id+"F20.wireOp",EDGE,"E52.9.10.0"),sQuery(id+"F20.wireOp",EDGE,"E52.12.10.0"),sQuery(id+"F20.wireOp",EDGE,"E52.16.10.0"),sQuery(id+"F20.wireOp",EDGE,"E52.19.10.0"),sQuery(id+"F20.wireOp",EDGE,"E52.2.11.0"),sQuery(id+"F20.wireOp",EDGE,"E52.3.11.0"),sQuery(id+"F20.wireOp",EDGE,"E52.6.11.0"),sQuery(id+"F20.wireOp",EDGE,"E52.9.11.0"),sQuery(id+"F20.wireOp",EDGE,"E52.12.11.0"),sQuery(id+"F20.wireOp",EDGE,"E52.16.11.0"),sQuery(id+"F20.wireOp",EDGE,"E52.19.11.0"),sQuery(id+"F20.wireOp",EDGE,"E52.2.12.0"),sQuery(id+"F20.wireOp",EDGE,"E52.3.12.0"),sQuery(id+"F20.wireOp",EDGE,"E52.6.12.0"),sQuery(id+"F20.wireOp",EDGE,"E52.9.12.0"),sQuery(id+"F20.wireOp",EDGE,"E52.12.12.0"),sQuery(id+"F20.wireOp",EDGE,"E52.16.12.0"),sQuery(id+"F20.wireOp",EDGE,"E52.19.12.0")])],"isStart":true});
            extrude(context, id + "F25", {"entities" : qUnion([Q0]), "operationType" : NewBodyOperationType.REMOVE, "endBound" : BoundingType.UP_TO_SURFACE, "oppositeDirection" : true, "endBoundEntityFace" : qUnion([Q1]), "depth" : 25.4 * mm});
        }
        {
            var Q0;
            Q0=makeQuery(id+"F21.opExtrude","CAP_EDGE",EDGE,{"disambiguationData":[OSD([sQuery(id+"F20.wireOp",EDGE,"E52.3.6.0")])],"isStart":false});
            var Q1;
            Q1=makeQuery(id+"F21.opExtrude","CAP_EDGE",EDGE,{"disambiguationData":[OSD([sQuery(id+"F20.wireOp",EDGE,"E52.6.5.0")])],"isStart":false});
            var Q2;
            Q2=makeQuery(id+"F21.opExtrude","CAP_EDGE",EDGE,{"disambiguationData":[OSD([sQuery(id+"F20.wireOp",EDGE,"E52.3.5.0")])],"isStart":false});
            var Q3;
            Q3=makeQuery(id+"F21.opExtrude","CAP_EDGE",EDGE,{"disambiguationData":[OSD([sQuery(id+"F20.wireOp",EDGE,"E52.6.4.0")])],"isStart":false});
            var Q4;
            Q4=makeQuery(id+"F21.opExtrude","CAP_EDGE",EDGE,{"disambiguationData":[OSD([sQuery(id+"F20.wireOp",EDGE,"E52.3.4.0")])],"isStart":false});
            var Q5;
            Q5=makeQuery(id+"F21.opExtrude","CAP_EDGE",EDGE,{"disambiguationData":[OSD([sQuery(id+"F20.wireOp",EDGE,"E52.6.3.0")])],"isStart":false});
            var Q6;
            Q6=makeQuery(id+"F21.opExtrude","CAP_EDGE",EDGE,{"disambiguationData":[OSD([sQuery(id+"F20.wireOp",EDGE,"E52.3.3.0")])],"isStart":false});
            var Q7;
            Q7=makeQuery(id+"F21.opExtrude","CAP_EDGE",EDGE,{"disambiguationData":[OSD([sQuery(id+"F20.wireOp",EDGE,"E51.2.2")])],"isStart":false});
            var Q8;
            Q8=makeQuery(id+"F21.opExtrude","CAP_EDGE",EDGE,{"disambiguationData":[OSD([sQuery(id+"F20.wireOp",EDGE,"E51.2.1")])],"isStart":false});
            var Q9;
            Q9=makeQuery(id+"F21.opExtrude","CAP_EDGE",EDGE,{"disambiguationData":[OSD([sQuery(id+"F20.wireOp",EDGE,"E51.1.2")])],"isStart":false});
            var Q10;
            Q10=makeQuery(id+"F21.opExtrude","CAP_EDGE",EDGE,{"disambiguationData":[OSD([sQuery(id+"F20.wireOp",EDGE,"E51.1.1")])],"isStart":false});
            var Q11;
            Q11=makeQuery(id+"F21.opExtrude","CAP_EDGE",EDGE,{"disambiguationData":[OSD([sQuery(id+"F20.wireOp",EDGE,"E47")])],"isStart":false});
            var Q12;
            Q12=makeQuery(id+"F21.opExtrude","CAP_EDGE",EDGE,{"disambiguationData":[OSD([sQuery(id+"F20.wireOp",EDGE,"E49.MirrorCS")])],"isStart":false});
            var Q13;
            Q13=makeQuery(id+"F21.opExtrude","CAP_EDGE",EDGE,{"disambiguationData":[OSD([sQuery(id+"F20.wireOp",EDGE,"E52.6.12.0")])],"isStart":false});
            var Q14;
            Q14=makeQuery(id+"F21.opExtrude","CAP_EDGE",EDGE,{"disambiguationData":[OSD([sQuery(id+"F20.wireOp",EDGE,"E52.3.12.0")])],"isStart":false});
            var Q15;
            Q15=makeQuery(id+"F21.opExtrude","CAP_EDGE",EDGE,{"disambiguationData":[OSD([sQuery(id+"F20.wireOp",EDGE,"E52.6.11.0")])],"isStart":false});
            var Q16;
            Q16=makeQuery(id+"F21.opExtrude","CAP_EDGE",EDGE,{"disambiguationData":[OSD([sQuery(id+"F20.wireOp",EDGE,"E52.3.11.0")])],"isStart":false});
            var Q17;
            Q17=makeQuery(id+"F21.opExtrude","CAP_EDGE",EDGE,{"disambiguationData":[OSD([sQuery(id+"F20.wireOp",EDGE,"E52.6.10.0")])],"isStart":false});
            var Q18;
            Q18=makeQuery(id+"F21.opExtrude","CAP_EDGE",EDGE,{"disambiguationData":[OSD([sQuery(id+"F20.wireOp",EDGE,"E52.3.10.0")])],"isStart":false});
            var Q19;
            Q19=makeQuery(id+"F21.opExtrude","CAP_EDGE",EDGE,{"disambiguationData":[OSD([sQuery(id+"F20.wireOp",EDGE,"E52.6.9.0")])],"isStart":false});
            var Q20;
            Q20=makeQuery(id+"F21.opExtrude","CAP_EDGE",EDGE,{"disambiguationData":[OSD([sQuery(id+"F20.wireOp",EDGE,"E52.3.9.0")])],"isStart":false});
            var Q21;
            Q21=makeQuery(id+"F21.opExtrude","CAP_EDGE",EDGE,{"disambiguationData":[OSD([sQuery(id+"F20.wireOp",EDGE,"E52.6.8.0")])],"isStart":false});
            var Q22;
            Q22=makeQuery(id+"F21.opExtrude","CAP_EDGE",EDGE,{"disambiguationData":[OSD([sQuery(id+"F20.wireOp",EDGE,"E52.3.8.0")])],"isStart":false});
            var Q23;
            Q23=makeQuery(id+"F21.opExtrude","CAP_EDGE",EDGE,{"disambiguationData":[OSD([sQuery(id+"F20.wireOp",EDGE,"E52.6.7.0")])],"isStart":false});
            var Q24;
            Q24=makeQuery(id+"F21.opExtrude","CAP_EDGE",EDGE,{"disambiguationData":[OSD([sQuery(id+"F20.wireOp",EDGE,"E52.3.7.0")])],"isStart":false});
            var Q25;
            Q25=makeQuery(id+"F21.opExtrude","CAP_EDGE",EDGE,{"disambiguationData":[OSD([sQuery(id+"F20.wireOp",EDGE,"E52.6.6.0")])],"isStart":false});
            var Q26;
            Q26=makeQuery(id+"F21.opExtrude","CAP_EDGE",EDGE,{"disambiguationData":[OSD([sQuery(id+"F20.wireOp",EDGE,"E52.3.9.0")])],"isStart":true});
            var Q27;
            Q27=makeQuery(id+"F21.opExtrude","CAP_EDGE",EDGE,{"disambiguationData":[OSD([sQuery(id+"F20.wireOp",EDGE,"E52.6.9.0")])],"isStart":true});
            var Q28;
            Q28=makeQuery(id+"F21.opExtrude","CAP_EDGE",EDGE,{"disambiguationData":[OSD([sQuery(id+"F20.wireOp",EDGE,"E52.3.10.0")])],"isStart":true});
            var Q29;
            Q29=makeQuery(id+"F21.opExtrude","CAP_EDGE",EDGE,{"disambiguationData":[OSD([sQuery(id+"F20.wireOp",EDGE,"E52.6.10.0")])],"isStart":true});
            var Q30;
            Q30=makeQuery(id+"F21.opExtrude","CAP_EDGE",EDGE,{"disambiguationData":[OSD([sQuery(id+"F20.wireOp",EDGE,"E52.3.11.0")])],"isStart":true});
            var Q31;
            Q31=makeQuery(id+"F21.opExtrude","CAP_EDGE",EDGE,{"disambiguationData":[OSD([sQuery(id+"F20.wireOp",EDGE,"E52.6.11.0")])],"isStart":true});
            var Q32;
            Q32=makeQuery(id+"F21.opExtrude","CAP_EDGE",EDGE,{"disambiguationData":[OSD([sQuery(id+"F20.wireOp",EDGE,"E52.3.12.0")])],"isStart":true});
            var Q33;
            Q33=makeQuery(id+"F21.opExtrude","CAP_EDGE",EDGE,{"disambiguationData":[OSD([sQuery(id+"F20.wireOp",EDGE,"E52.6.12.0")])],"isStart":true});
            var Q34;
            Q34=makeQuery(id+"F21.opExtrude","CAP_EDGE",EDGE,{"disambiguationData":[OSD([sQuery(id+"F20.wireOp",EDGE,"E49.MirrorCS")])],"isStart":true});
            var Q35;
            Q35=makeQuery(id+"F21.opExtrude","CAP_EDGE",EDGE,{"disambiguationData":[OSD([sQuery(id+"F20.wireOp",EDGE,"E47")])],"isStart":true});
            var Q36;
            Q36=makeQuery(id+"F21.opExtrude","CAP_EDGE",EDGE,{"disambiguationData":[OSD([sQuery(id+"F20.wireOp",EDGE,"E51.1.1")])],"isStart":true});
            var Q37;
            Q37=makeQuery(id+"F21.opExtrude","CAP_EDGE",EDGE,{"disambiguationData":[OSD([sQuery(id+"F20.wireOp",EDGE,"E51.1.2")])],"isStart":true});
            var Q38;
            Q38=makeQuery(id+"F21.opExtrude","CAP_EDGE",EDGE,{"disambiguationData":[OSD([sQuery(id+"F20.wireOp",EDGE,"E51.2.1")])],"isStart":true});
            var Q39;
            Q39=makeQuery(id+"F21.opExtrude","CAP_EDGE",EDGE,{"disambiguationData":[OSD([sQuery(id+"F20.wireOp",EDGE,"E51.2.2")])],"isStart":true});
            var Q40;
            Q40=makeQuery(id+"F21.opExtrude","CAP_EDGE",EDGE,{"disambiguationData":[OSD([sQuery(id+"F20.wireOp",EDGE,"E52.3.3.0")])],"isStart":true});
            var Q41;
            Q41=makeQuery(id+"F21.opExtrude","CAP_EDGE",EDGE,{"disambiguationData":[OSD([sQuery(id+"F20.wireOp",EDGE,"E52.6.3.0")])],"isStart":true});
            var Q42;
            Q42=makeQuery(id+"F21.opExtrude","CAP_EDGE",EDGE,{"disambiguationData":[OSD([sQuery(id+"F20.wireOp",EDGE,"E52.3.4.0")])],"isStart":true});
            var Q43;
            Q43=makeQuery(id+"F21.opExtrude","CAP_EDGE",EDGE,{"disambiguationData":[OSD([sQuery(id+"F20.wireOp",EDGE,"E52.6.4.0")])],"isStart":true});
            var Q44;
            Q44=makeQuery(id+"F21.opExtrude","CAP_EDGE",EDGE,{"disambiguationData":[OSD([sQuery(id+"F20.wireOp",EDGE,"E52.3.5.0")])],"isStart":true});
            var Q45;
            Q45=makeQuery(id+"F21.opExtrude","CAP_EDGE",EDGE,{"disambiguationData":[OSD([sQuery(id+"F20.wireOp",EDGE,"E52.6.5.0")])],"isStart":true});
            var Q46;
            Q46=makeQuery(id+"F21.opExtrude","CAP_EDGE",EDGE,{"disambiguationData":[OSD([sQuery(id+"F20.wireOp",EDGE,"E52.3.6.0")])],"isStart":true});
            var Q47;
            Q47=makeQuery(id+"F21.opExtrude","CAP_EDGE",EDGE,{"disambiguationData":[OSD([sQuery(id+"F20.wireOp",EDGE,"E52.6.6.0")])],"isStart":true});
            var Q48;
            Q48=makeQuery(id+"F21.opExtrude","CAP_EDGE",EDGE,{"disambiguationData":[OSD([sQuery(id+"F20.wireOp",EDGE,"E52.3.7.0")])],"isStart":true});
            var Q49;
            Q49=makeQuery(id+"F21.opExtrude","CAP_EDGE",EDGE,{"disambiguationData":[OSD([sQuery(id+"F20.wireOp",EDGE,"E52.6.7.0")])],"isStart":true});
            var Q50;
            Q50=makeQuery(id+"F21.opExtrude","CAP_EDGE",EDGE,{"disambiguationData":[OSD([sQuery(id+"F20.wireOp",EDGE,"E52.3.8.0")])],"isStart":true});
            var Q51;
            Q51=makeQuery(id+"F21.opExtrude","CAP_EDGE",EDGE,{"disambiguationData":[OSD([sQuery(id+"F20.wireOp",EDGE,"E52.6.8.0")])],"isStart":true});
            fillet(context, id + "F26", {"entities" : qUnion([Q0, Q1, Q2, Q3, Q4, Q5, Q6, Q7, Q8, Q9, Q10, Q11, Q12, Q13, Q14, Q15, Q16, Q17, Q18, Q19, Q20, Q21, Q22, Q23, Q24, Q25, Q26, Q27, Q28, Q29, Q30, Q31, Q32, Q33, Q34, Q35, Q36, Q37, Q38, Q39, Q40, Q41, Q42, Q43, Q44, Q45, Q46, Q47, Q48, Q49, Q50, Q51]), "radius" : 2 * mm, "allowEdgeOverflow" : false});
        }
        {
            var Q0;
            Q0=qCreatedBy(makeId("Front.planeOp"),FACE);
            var sketch = newSketch(context, id + "F27", { "sketchPlane" : qUnion([Q0])});
            skLineSegment(sketch, "E55", {"start": v(-7.5, 5.5) * mm, "end": v(-7.5, 9.5) * mm});
            skLineSegment(sketch, "E56", {"start": v(-7, 10) * mm, "end": v(-6, 10) * mm});
            skLineSegment(sketch, "E57", {"start": v(-2.5, 9.7) * mm, "end": v(-2.5, 5.3) * mm});
            skLineSegment(sketch, "E58", {"start": v(-2.8, 5) * mm, "end": v(-3.5, 5) * mm});
            skPoint(sketch, "E59.visualSharp", {"position": v(-7.5, 10) * mm});
            skArc(sketch, "E59.filletArc", {"start": v(-7, 10) * mm, "mid": v(-7.35, 9.85) * mm, "end": v(-7.5, 9.5) * mm});
            skPoint(sketch, "E60.visualSharp", {"position": v(-7.5, 5) * mm});
            skArc(sketch, "E60.filletArc", {"start": v(-7.5, 5.5) * mm, "mid": v(-7.35, 5.15) * mm, "end": v(-7, 5) * mm});
            skLineSegment(sketch, "E61", {"start": v(-2.8, 10) * mm, "end": v(-2.5, 9.7) * mm});
            skLineSegment(sketch, "E62", {"start": v(-3.5, 10) * mm, "end": v(-3.5, 9.8) * mm});
            skLineSegment(sketch, "E63", {"start": v(-3.5, 9.8) * mm, "end": v(-6, 9.8) * mm});
            skLineSegment(sketch, "E64", {"start": v(-6, 9.8) * mm, "end": v(-6, 10) * mm});
            skLineSegment(sketch, "E65.trimOffspring", {"start": v(-3.5, 10) * mm, "end": v(-2.8, 10) * mm});
            skLineSegment(sketch, "E66", {"start": v(-7.5, 7.5) * mm, "end": v(0, 7.5) * mm, "construction": true});
            skLineSegment(sketch, "E67.MirrorCS", {"start": v(-2.8, 5) * mm, "end": v(-2.5, 5.3) * mm});
            skLineSegment(sketch, "E68.MirrorCS", {"start": v(-3.5, 5) * mm, "end": v(-3.5, 5.2) * mm});
            skLineSegment(sketch, "E69.MirrorCS", {"start": v(-6, 5.2) * mm, "end": v(-6, 5) * mm});
            skLineSegment(sketch, "E70.MirrorCS", {"start": v(-3.5, 5.2) * mm, "end": v(-6, 5.2) * mm});
            skLineSegment(sketch, "E71.trimOffspring", {"start": v(-6, 5) * mm, "end": v(-7, 5) * mm});
            skPoint(sketch, "E72.orphan", {"position": v(-2.5, 5) * mm});
            skLineSegment(sketch, "E73", {"start": v(0, 10.77) * mm, "end": v(0, 4.26) * mm, "construction": true});
            skSolve(sketch);
        }
        {
            var Q0;
            Q0 = qSketchRegion(id + "F27", true);
            var Q1;
            Q1=sQuery(id+"F27.wireOp",EDGE,"E73");
            revolve(context, id + "F28", {"entities" : qUnion([Q0]), "axis" : qUnion([Q1]), "revolveType" : RevolveType.FULL});
        }
        {
            var Q0;
            Q0=makeQuery(id+"F28.opRevolve","SWEPT_BODY",BODY,{"disambiguationData":[OSD([sQuery(id+"F27.wireOp",EDGE,"E55"),sQuery(id+"F27.wireOp",EDGE,"E56"),sQuery(id+"F27.wireOp",EDGE,"E57"),sQuery(id+"F27.wireOp",EDGE,"E58"),sQuery(id+"F27.wireOp",EDGE,"E59.filletArc"),sQuery(id+"F27.wireOp",EDGE,"E60.filletArc"),sQuery(id+"F27.wireOp",EDGE,"E61"),sQuery(id+"F27.wireOp",EDGE,"E62"),sQuery(id+"F27.wireOp",EDGE,"E63"),sQuery(id+"F27.wireOp",EDGE,"E64"),sQuery(id+"F27.wireOp",EDGE,"E65.trimOffspring"),sQuery(id+"F27.wireOp",EDGE,"E67.MirrorCS"),sQuery(id+"F27.wireOp",EDGE,"E68.MirrorCS"),sQuery(id+"F27.wireOp",EDGE,"E69.MirrorCS"),sQuery(id+"F27.wireOp",EDGE,"E70.MirrorCS"),sQuery(id+"F27.wireOp",EDGE,"E71.trimOffspring")])]});
            transform(context, id + "F29", {"entities" : qUnion([Q0]), "transformType" : TransformType.TRANSLATION_3D, "dx" : 0 * mm, "dy" : 0 * mm, "dz" : -12 * mm, "makeCopy" : true});
        }
    });
